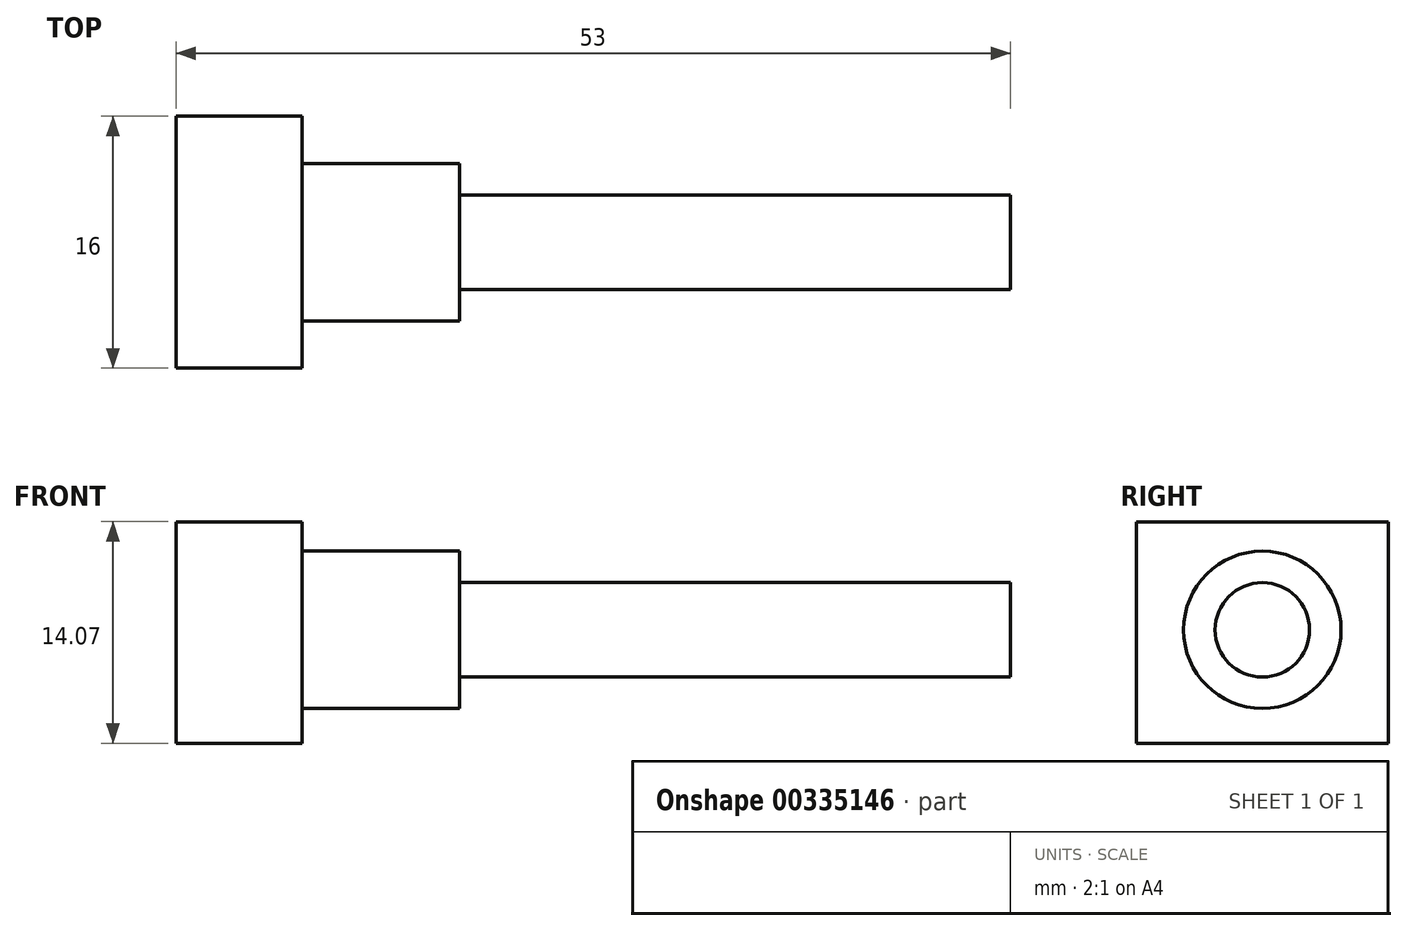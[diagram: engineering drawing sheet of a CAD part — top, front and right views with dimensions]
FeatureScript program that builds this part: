
annotation { "Feature Type Name" : "Feature", "Feature Type Description" : "" }
export const myFeature = defineFeature(function(context is Context, id is Id, definition is map)
    precondition{}
    {
        {
            var Q0;
            Q0=qCreatedBy(makeId("Right.planeOp"),FACE);
            var sketch = newSketch(context, id + "F0", { "sketchPlane" : qUnion([Q0])});
            skCircle(sketch, "E0", {"center": v(0, 0) * mm, "radius": 5 * mm});
            skSolve(sketch);
        }
        {
            var Q0;
            Q0 = qSketchRegion(id + "F0", true);
            extrude(context, id + "F1", {"entities" : qUnion([Q0]), "depth" : 10 * mm});
        }
        {
            var Q0;
            Q0=makeQuery(id+"F1.opExtrude","CAP_FACE",FACE,{"disambiguationData":[OSD([sQuery(id+"F0.wireOp",EDGE,"E0")])],"isStart":false});
            var sketch = newSketch(context, id + "F2", { "sketchPlane" : qUnion([Q0])});
            skCircle(sketch, "E1", {"center": v(0, 0) * mm, "radius": 3 * mm});
            skSolve(sketch);
        }
        {
            var Q0;
            Q0 = qSketchRegion(id + "F2", true);
            extrude(context, id + "F3", {"entities" : qUnion([Q0]), "operationType" : NewBodyOperationType.ADD, "depth" : 35 * mm});
        }
        {
            var Q0;
            Q0=makeQuery(id+"F1.opExtrude","CAP_FACE",FACE,{"disambiguationData":[OSD([sQuery(id+"F0.wireOp",EDGE,"E0")])],"isStart":true});
            var sketch = newSketch(context, id + "F4", { "sketchPlane" : qUnion([Q0])});
            skLineSegment(sketch, "E2.bottom", {"start": v(-8, 6.87) * mm, "end": v(8, 6.87) * mm});
            skLineSegment(sketch, "E2.top", {"start": v(-8, -7.2) * mm, "end": v(8, -7.2) * mm});
            skLineSegment(sketch, "E2.left", {"start": v(-8, 6.87) * mm, "end": v(-8, -7.2) * mm});
            skLineSegment(sketch, "E2.right", {"start": v(8, 6.87) * mm, "end": v(8, -7.2) * mm});
            skSolve(sketch);
        }
        {
            var Q0;
            Q0 = qSketchRegion(id + "F4", true);
            extrude(context, id + "F5", {"entities" : qUnion([Q0]), "operationType" : NewBodyOperationType.ADD, "depth" : 8 * mm});
        }
    });
